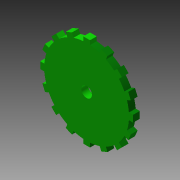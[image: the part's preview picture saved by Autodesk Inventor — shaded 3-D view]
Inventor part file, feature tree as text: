
AUTODESK INVENTOR PART (.ipt)
format: ipt  version: 2015 (Build 190159000, 159)  size: 159,232 bytes
history: native  units: in
note: dims shown in document units (in); Inventor stores cm internally (conversion verified against a paired STEP export)
features: extrude x2, sketch x1, pattern_circular x1
ambient origin geometry x8: Origin, YZ Plane, XZ Plane, XY Plane, X Axis, Y Axis, Z Axis, Center Point
bodies: Solid1 (feature_tree)
feature tree (4):
  sketch  "Sketch1"  dims[d0=0.03in d2=0.025in d3=0.025in d4=0.63in d5=0.079in d6=0.05in d7=0.0in d8=0.05in d9=0.0in d10=6.2992in d11=360.0deg]
  extrude  "Extrusion1"  Depth=0.025in
  extrude  "Extrusion2"  Depth=0.025in
  pattern_circular  "Circular Pattern1"  [2 undecoded]
note: 2 required parameter values undecoded (feature->parameter linkage not recoverable at this tier; creation-order binding heuristic only, values carry confidence <= 0.55)
